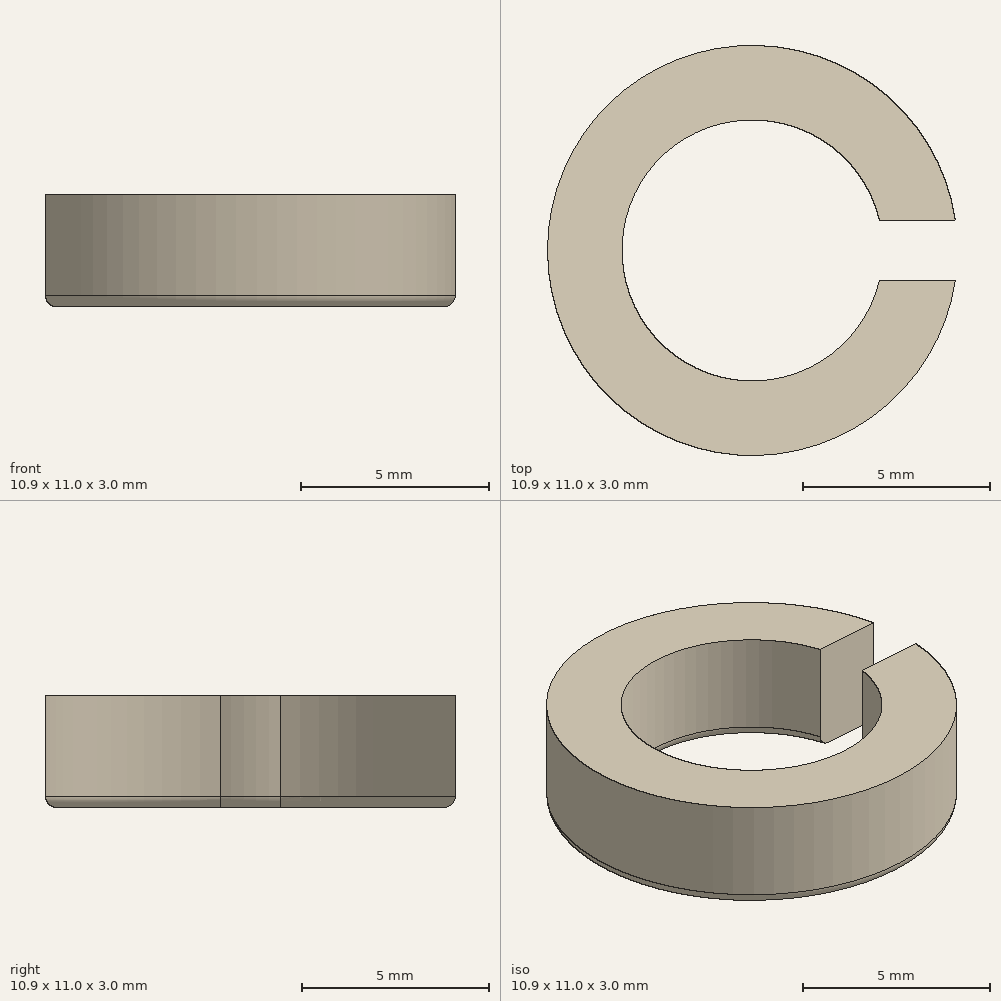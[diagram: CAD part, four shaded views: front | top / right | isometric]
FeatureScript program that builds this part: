
annotation { "Feature Type Name" : "Feature", "Feature Type Description" : "" }
export const myFeature = defineFeature(function(context is Context, id is Id, definition is map)
    precondition{}
    {
        {
            var Q0;
            Q0=qCreatedBy(makeId("Front.planeOp"),FACE);
            var sketch = newSketch(context, id + "F0", { "sketchPlane" : qUnion([Q0])});
            skLineSegment(sketch, "E0.bottom", {"start": v(3.8, 0) * mm, "end": v(5.2, 0) * mm});
            skLineSegment(sketch, "E0.top", {"start": v(3.5, 3) * mm, "end": v(5.5, 3) * mm});
            skLineSegment(sketch, "E0.left", {"start": v(3.5, 0.3) * mm, "end": v(3.5, 3) * mm});
            skLineSegment(sketch, "E0.right", {"start": v(5.5, 0.3) * mm, "end": v(5.5, 3) * mm});
            skPoint(sketch, "E1.visualSharp", {"position": v(3.5, 3) * mm});
            skLineSegment(sketch, "E1.filletArc", {"start": v(3.5, 3) * mm, "end": v(3.5, 3) * mm});
            skPoint(sketch, "E2.visualSharp", {"position": v(3.5, 0) * mm});
            skLineSegment(sketch, "E2.filletArc", {"start": v(3.5, 0) * mm, "end": v(3.5, 0) * mm});
            skPoint(sketch, "E3.visualSharp", {"position": v(5.5, 3) * mm});
            skLineSegment(sketch, "E3.filletArc", {"start": v(5.5, 3) * mm, "end": v(5.5, 3) * mm});
            skPoint(sketch, "E4.visualSharp", {"position": v(5.5, 0) * mm});
            skLineSegment(sketch, "E4.filletArc", {"start": v(5.5, 0) * mm, "end": v(5.5, 0) * mm});
            skLineSegment(sketch, "E5", {"start": v(0, 0) * mm, "end": v(0, 7.7) * mm});
            skArc(sketch, "E6.filletArc", {"start": v(3.5, 0.3) * mm, "mid": v(3.59, 0.09) * mm, "end": v(3.8, 0) * mm});
            skArc(sketch, "E7.filletArc", {"start": v(5.2, 0) * mm, "mid": v(5.41, 0.09) * mm, "end": v(5.5, 0.3) * mm});
            skSolve(sketch);
        }
        {
            var Q0;
            Q0=makeQuery(id+"F0.imprint","IMPRINT",FACE,{"disambiguationData":[TD([[makeQuery(id+"F0.imprint","IMPRINT",EDGE,{"derivedFrom":sQuery(id+"F0.wireOp",EDGE,"E0.bottom")}),1.0]])]});
            var Q1;
            Q1=sQuery(id+"F0.wireOp",EDGE,"E5");
            revolve(context, id + "F1", {"entities" : qUnion([Q0]), "axis" : qUnion([Q1]), "revolveType" : RevolveType.FULL});
        }
        {
            var Q0;
            Q0=qCreatedBy(makeId("Top.planeOp"),FACE);
            var sketch = newSketch(context, id + "F2", { "sketchPlane" : qUnion([Q0])});
            skPoint(sketch, "E8", {"position": v(4.5, 0) * mm});
            skLineSegment(sketch, "E9.bottom", {"start": v(6.61, 0.8) * mm, "end": v(2.39, 0.8) * mm});
            skLineSegment(sketch, "E9.top", {"start": v(6.61, -0.8) * mm, "end": v(2.39, -0.8) * mm});
            skLineSegment(sketch, "E9.left", {"start": v(6.61, 0.8) * mm, "end": v(6.61, -0.8) * mm});
            skLineSegment(sketch, "E9.right", {"start": v(2.39, 0.8) * mm, "end": v(2.39, -0.8) * mm});
            skSolve(sketch);
        }
        {
            var Q0;
            Q0=makeQuery(id+"F2.imprint","IMPRINT",FACE,{"disambiguationData":[TD([[makeQuery(id+"F2.imprint","IMPRINT",EDGE,{"derivedFrom":sQuery(id+"F2.wireOp",EDGE,"E9.bottom")}),1.0]])]});
            extrude(context, id + "F3", {"entities" : qUnion([Q0]), "operationType" : NewBodyOperationType.REMOVE, "depth" : 4 * mm, "offsetDistance" : 25 * mm});
        }
    });
